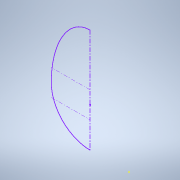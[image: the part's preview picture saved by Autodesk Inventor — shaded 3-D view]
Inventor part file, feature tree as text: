
AUTODESK INVENTOR PART (.ipt)
format: ipt  version: 2022 (Build 260153000, 153)  size: 87,040 bytes
history: native  units: in
note: dims shown in document units (in); Inventor stores cm internally (conversion verified against a paired STEP export)
features: sketch x1
ambient origin geometry x8: Origin, YZ Plane, XZ Plane, XY Plane, X Axis, Y Axis, Z Axis, Center Point
feature tree (1):
  sketch  "Sketch1"  dims[d3=0.0344in d4=0.0344in]
